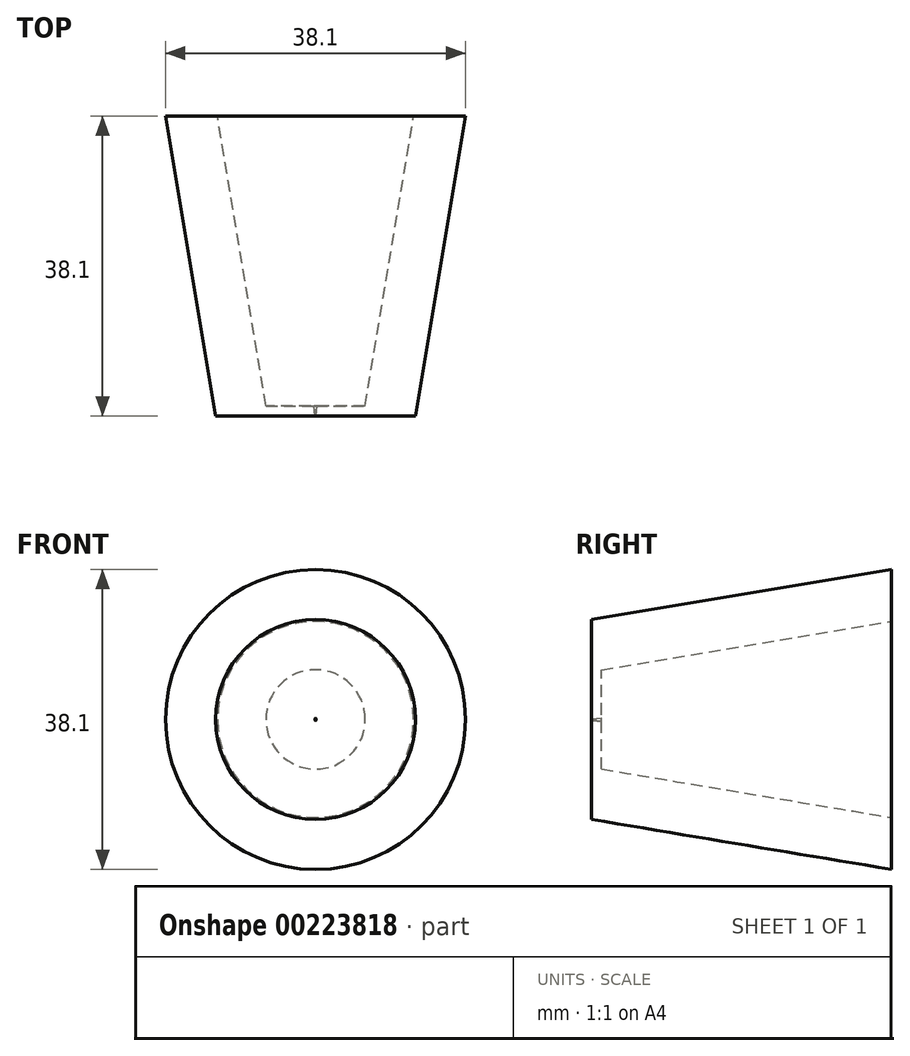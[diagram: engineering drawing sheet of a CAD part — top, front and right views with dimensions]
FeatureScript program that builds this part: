
annotation { "Feature Type Name" : "Feature", "Feature Type Description" : "" }
export const myFeature = defineFeature(function(context is Context, id is Id, definition is map)
    precondition{}
    {
        {
            var Q0;
            Q0=qCreatedBy(makeId("Top.planeOp"),FACE);
            var sketch = newSketch(context, id + "F0", { "sketchPlane" : qUnion([Q0])});
            skLineSegment(sketch, "E0", {"start": v(0, 0) * mm, "end": v(0, 38.1) * mm});
            skLineSegment(sketch, "E1", {"start": v(0, 0) * mm, "end": v(-12.7, 0) * mm});
            skLineSegment(sketch, "E2", {"start": v(0, 38.1) * mm, "end": v(-19.05, 38.1) * mm});
            skLineSegment(sketch, "E3", {"start": v(-19.05, 38.1) * mm, "end": v(-12.7, 0) * mm});
            skLineSegment(sketch, "E4", {"start": v(0, 38.1) * mm, "end": v(0, 12.7) * mm});
            skLineSegment(sketch, "E5", {"start": v(0, 38.1) * mm, "end": v(-6.35, 38.1) * mm});
            skLineSegment(sketch, "E6", {"start": v(-12.45, 38.1) * mm, "end": v(-6.3, 1.28) * mm});
            skLineSegment(sketch, "E7", {"start": v(-0.21, 1.28) * mm, "end": v(0, -1.05) * mm});
            skLineSegment(sketch, "E8", {"start": v(-6.3, 1.28) * mm, "end": v(-0.21, 1.28) * mm});
            skSolve(sketch);
        }
        {
            var Q0;
            {var subQ1=sQuery(id+"F0.wireOp",EDGE,"E3");Q0=makeQuery(id+"F0.imprint","IMPRINT",FACE,{"disambiguationData":[TD([[makeQuery(id+"F0.imprint","IMPRINT",EDGE,{"derivedFrom":subQ1}),1.0]])]});}
            var Q1;
            Q1=sQuery(id+"F0.wireOp",EDGE,"E4");
            revolve(context, id + "F1", {"entities" : qUnion([Q0]), "axis" : qUnion([Q1]), "revolveType" : RevolveType.FULL, "oppositeDirection" : true});
        }
    });
